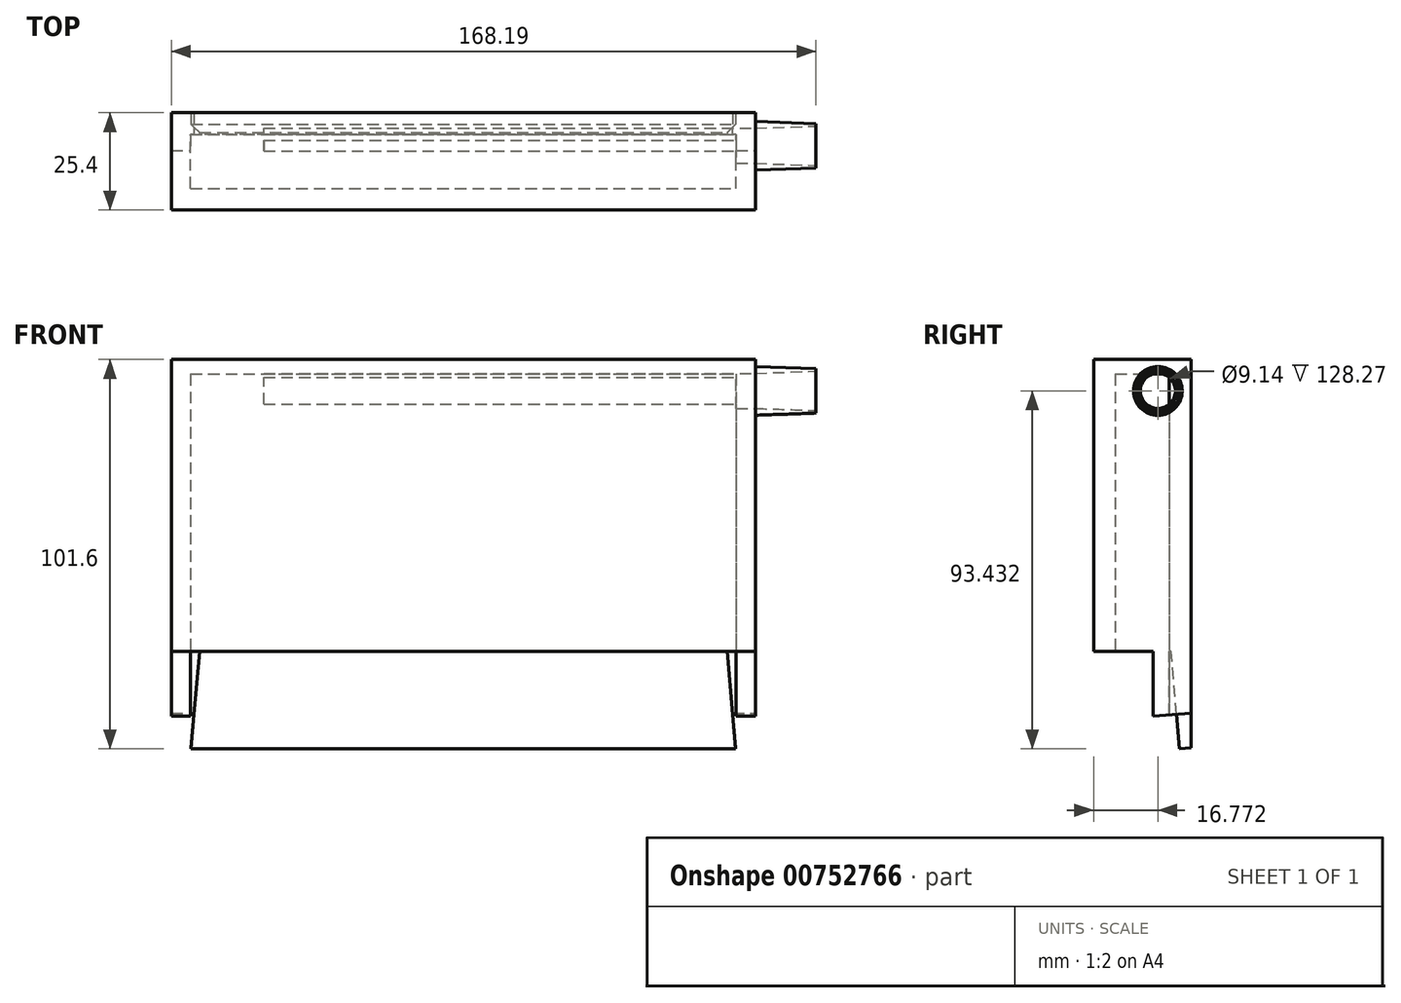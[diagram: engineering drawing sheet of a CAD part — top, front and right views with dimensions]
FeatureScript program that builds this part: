
annotation { "Feature Type Name" : "Feature", "Feature Type Description" : "" }
export const myFeature = defineFeature(function(context is Context, id is Id, definition is map)
    precondition{}
    {
        {
            var Q0;
            Q0=qCreatedBy(makeId("Front.planeOp"),FACE);
            var sketch = newSketch(context, id + "F0", { "sketchPlane" : qUnion([Q0])});
            skLineSegment(sketch, "E0.bottom", {"start": v(-76.2, 38.1) * mm, "end": v(76.2, 38.1) * mm});
            skLineSegment(sketch, "E0.top", {"start": v(-76.2, -38.1) * mm, "end": v(76.2, -38.1) * mm});
            skLineSegment(sketch, "E0.left", {"start": v(-76.2, 38.1) * mm, "end": v(-76.2, -38.1) * mm});
            skLineSegment(sketch, "E0.right", {"start": v(76.2, 38.1) * mm, "end": v(76.2, -38.1) * mm});
            skPoint(sketch, "E0.middle", {"position": v(0, 0) * mm});
            skLineSegment(sketch, "E1", {"start": v(-76.2, -34.16) * mm, "end": v(76.2, -34.16) * mm});
            skSolve(sketch);
        }
        {
            var Q0;
            {var subQ0=sQuery(id+"F0.wireOp",EDGE,"E0.bottom");Q0=makeQuery(id+"F0.imprint","IMPRINT",FACE,{"disambiguationData":[TD([[makeQuery(id+"F0.imprint","IMPRINT",EDGE,{"derivedFrom":subQ0}),-1.0]])]});}
            var Q1;
            {var subQ0=sQuery(id+"F0.wireOp",EDGE,"E0.top");Q1=makeQuery(id+"F0.imprint","IMPRINT",FACE,{"disambiguationData":[TD([[makeQuery(id+"F0.imprint","IMPRINT",EDGE,{"derivedFrom":subQ0}),1.0]])]});}
            extrude(context, id + "F1", {"entities" : qUnion([Q0, Q1]), "depth" : 25.4 * mm, "offsetDistance" : 25.4 * mm});
        }
        {
            var Q0;
            Q0=makeQuery(id+"F1.opExtrude","SWEPT_FACE",FACE,{"disambiguationData":[OSD([sQuery(id+"F0.wireOp",EDGE,"E0.right")])]});
            var sketch = newSketch(context, id + "F2", { "sketchPlane" : qUnion([Q0])});
            skCircle(sketch, "E2", {"center": v(-8.63, 29.93) * mm, "radius": 6.35 * mm});
            skCircle(sketch, "E3", {"center": v(-8.63, 29.93) * mm, "radius": 4.57 * mm});
            skSolve(sketch);
        }
        {
            var Q0;
            Q0=makeQuery(id+"F2.imprint","IMPRINT",FACE,{"disambiguationData":[TD([[makeQuery(id+"F2.imprint","IMPRINT",EDGE,{"derivedFrom":sQuery(id+"F2.wireOp",EDGE,"E3")}),1.0]])]});
            extrude(context, id + "F3", {"entities" : qUnion([Q0]), "operationType" : NewBodyOperationType.REMOVE, "oppositeDirection" : true, "depth" : 128.27 * mm, "offsetDistance" : 25.4 * mm});
        }
        {
            var Q0;
            Q0 = qSketchRegion(id + "F2", true);
            extrude(context, id + "F4", {"entities" : qUnion([Q0]), "operationType" : NewBodyOperationType.ADD, "depth" : 25.4 * mm, "offsetDistance" : 25.4 * mm, "hasDraft" : true, "draftAngle" : 2 * degree, "draftPullDirection" : true});
        }
        {
            var Q0;
            Q0=makeQuery(id+"F1.opExtrude","SWEPT_FACE",FACE,{"disambiguationData":[OSD([sQuery(id+"F0.wireOp",EDGE,"E0.top")])]});
            var sketch = newSketch(context, id + "F5", { "sketchPlane" : qUnion([Q0])});
            skLineSegment(sketch, "E4.bottom", {"start": v(-71.2, 19.71) * mm, "end": v(71.2, 19.71) * mm});
            skLineSegment(sketch, "E4.top", {"start": v(-71.2, 5.69) * mm, "end": v(71.2, 5.69) * mm});
            skLineSegment(sketch, "E4.left", {"start": v(-71.2, 19.71) * mm, "end": v(-71.2, 5.69) * mm});
            skLineSegment(sketch, "E4.right", {"start": v(71.2, 19.71) * mm, "end": v(71.2, 5.69) * mm});
            skPoint(sketch, "E4.middle", {"position": v(0, 12.7) * mm});
            skPoint(sketch, "E4.middle.positionSnap0", {"position": v(-76.2, 12.7) * mm});
            skPoint(sketch, "E4.centerSnap0", {"position": v(-76.2, 12.7) * mm});
            skSolve(sketch);
        }
        {
            var Q0;
            Q0=makeQuery(id+"F5.imprint","IMPRINT",FACE,{"disambiguationData":[TD([[makeQuery(id+"F5.imprint","IMPRINT",EDGE,{"derivedFrom":sQuery(id+"F5.wireOp",EDGE,"E4.bottom")}),-1.0]])]});
            extrude(context, id + "F6", {"entities" : qUnion([Q0]), "operationType" : NewBodyOperationType.REMOVE, "oppositeDirection" : true, "depth" : 72.39 * mm, "offsetDistance" : 25.4 * mm});
        }
        {
            var Q0;
            Q0=qCreatedBy(makeId("Front.planeOp"),FACE);
            var sketch = newSketch(context, id + "F7", { "sketchPlane" : qUnion([Q0])});
            skLineSegment(sketch, "E5.bottom", {"start": v(92, 10.22) * mm, "end": v(133.43, 10.22) * mm});
            skLineSegment(sketch, "E5.top", {"start": v(92, 52.24) * mm, "end": v(133.43, 52.24) * mm});
            skLineSegment(sketch, "E5.left", {"start": v(92, 10.22) * mm, "end": v(92, 52.24) * mm});
            skLineSegment(sketch, "E5.right", {"start": v(133.43, 10.22) * mm, "end": v(133.43, 52.24) * mm});
            skPoint(sketch, "E5.middle", {"position": v(112.71, 31.23) * mm});
            skSolve(sketch);
        }
        {
            var Q0;
            Q0=makeQuery(id+"F7.imprint","IMPRINT",FACE,{"disambiguationData":[TD([[makeQuery(id+"F7.imprint","IMPRINT",EDGE,{"derivedFrom":sQuery(id+"F7.wireOp",EDGE,"E5.bottom")}),1.0]])]});
            extrude(context, id + "F8", {"entities" : qUnion([Q0]), "operationType" : NewBodyOperationType.REMOVE, "endBound" : BoundingType.SYMMETRIC, "depth" : 68.58 * mm, "offsetDistance" : 25.4 * mm});
        }
        {
            var Q0;
            Q0=makeQuery(id+"F1.opExtrude","SWEPT_FACE",FACE,{"disambiguationData":[OSD([sQuery(id+"F0.wireOp",EDGE,"E0.top")])]});
            var sketch = newSketch(context, id + "F9", { "sketchPlane" : qUnion([Q0])});
            skLineSegment(sketch, "E6", {"start": v(-76.2, 9.88) * mm, "end": v(76.2, 9.88) * mm});
            skLineSegment(sketch, "E7", {"start": v(76.2, 9.88) * mm, "end": v(76.2, 0) * mm});
            skLineSegment(sketch, "E8", {"start": v(76.2, 0) * mm, "end": v(-76.2, 0) * mm});
            skLineSegment(sketch, "E9", {"start": v(-76.2, 0) * mm, "end": v(-76.2, 9.88) * mm});
            skSolve(sketch);
        }
        {
            var Q0;
            {var subQ0=sQuery(id+"F9.wireOp",EDGE,"E7");Q0=makeQuery(id+"F9.imprint","IMPRINT",FACE,{"disambiguationData":[TD([[makeQuery(id+"F9.imprint","IMPRINT",EDGE,{"derivedFrom":subQ0}),-1.0]])]});}
            var Q1;
            {var subQ5=makeQuery(id+"F6.boolean.opBoolean","COPY",EDGE,{"derivedFrom":makeQuery(id+"F6.opExtrude","CAP_EDGE",EDGE,{"disambiguationData":[OSD([sQuery(id+"F5.wireOp",EDGE,"E4.top")])],"isStart":true})});Q1=makeQuery(id+"F9.imprint","IMPRINT",FACE,{"disambiguationData":[TD([[makeQuery(id+"F9.imprint","IMPRINT",EDGE,{"derivedFrom":subQ5}),1.0]])]});}
            extrude(context, id + "F10", {"entities" : qUnion([Q0, Q1]), "operationType" : NewBodyOperationType.ADD, "depth" : 25.4 * mm, "offsetDistance" : 25.4 * mm});
        }
        {
            var Q0;
            Q0=makeQuery(id+"F10.opExtrude","CAP_FACE",FACE,{"disambiguationData":[OSD([sQuery(id+"F9.wireOp",EDGE,"E6"),sQuery(id+"F9.wireOp",EDGE,"E7"),sQuery(id+"F9.wireOp",EDGE,"E8"),sQuery(id+"F9.wireOp",EDGE,"E9")])],"isStart":false});
            var sketch = newSketch(context, id + "F11", { "sketchPlane" : qUnion([Q0])});
            skLineSegment(sketch, "E10.bottom", {"start": v(-71.06, 16.8) * mm, "end": v(71.06, 16.8) * mm});
            skLineSegment(sketch, "E10.top", {"start": v(-71.06, 2.96) * mm, "end": v(71.06, 2.96) * mm});
            skLineSegment(sketch, "E10.left", {"start": v(-71.06, 16.8) * mm, "end": v(-71.06, 2.96) * mm});
            skLineSegment(sketch, "E10.right", {"start": v(71.06, 16.8) * mm, "end": v(71.06, 2.96) * mm});
            skPoint(sketch, "E10.middle", {"position": v(0, 9.88) * mm});
            skSolve(sketch);
        }
        {
            var Q0;
            {var subQ0=sQuery(id+"F11.wireOp",EDGE,"E10.top");Q0=makeQuery(id+"F11.imprint","IMPRINT",FACE,{"disambiguationData":[TD([[makeQuery(id+"F11.imprint","IMPRINT",EDGE,{"derivedFrom":subQ0}),1.0]])]});}
            var Q1;
            {var subQ0=sQuery(id+"F11.wireOp",EDGE,"E10.bottom");Q1=makeQuery(id+"F11.imprint","IMPRINT",FACE,{"disambiguationData":[TD([[makeQuery(id+"F11.imprint","IMPRINT",EDGE,{"derivedFrom":subQ0}),-1.0]])]});}
            extrude(context, id + "F12", {"entities" : qUnion([Q0, Q1]), "operationType" : NewBodyOperationType.REMOVE, "oppositeDirection" : true, "depth" : 25.4 * mm, "offsetDistance" : 25.4 * mm, "hasDraft" : true, "draftAngle" : 5 * degree, "draftPullDirection" : true});
        }
        {
            var Q0;
            Q0=makeQuery(id+"F12.boolean.opBoolean","COPY",FACE,{"derivedFrom":makeQuery(id+"F12.opExtrude","SWEPT_FACE",FACE,{"disambiguationData":[OSD([sQuery(id+"F11.wireOp",EDGE,"E10.top")])]})});
            var sketch = newSketch(context, id + "F13", { "sketchPlane" : qUnion([Q0])});
            skLineSegment(sketch, "E11.bottom", {"start": v(-92.4, -53.9) * mm, "end": v(92.4, -53.9) * mm});
            skLineSegment(sketch, "E11.top", {"start": v(-92.4, -129.4) * mm, "end": v(92.4, -129.4) * mm});
            skLineSegment(sketch, "E11.left", {"start": v(-92.4, -53.9) * mm, "end": v(-92.4, -129.4) * mm});
            skLineSegment(sketch, "E11.right", {"start": v(92.4, -53.9) * mm, "end": v(92.4, -129.4) * mm});
            skPoint(sketch, "E11.middle", {"position": v(0, -91.66) * mm});
            skSolve(sketch);
        }
        {
            var Q0;
            Q0=makeQuery(id+"F13.imprint","IMPRINT",FACE,{"disambiguationData":[TD([[makeQuery(id+"F13.imprint","IMPRINT",EDGE,{"derivedFrom":sQuery(id+"F13.wireOp",EDGE,"E11.top")}),1.0]])]});
            var Q1;
            {var subQ1=sQuery(id+"F11.wireOp",EDGE,"E10.top");var subQ6=makeQuery(id+"F12.boolean.opBoolean","COPY",EDGE,{"derivedFrom":makeQuery(id+"F12.opExtrude","CAP_EDGE",EDGE,{"disambiguationData":[OSD([subQ1])],"isStart":true})});Q1=makeQuery(id+"F13.imprint","IMPRINT",FACE,{"disambiguationData":[TD([[makeQuery(id+"F13.imprint","IMPRINT",EDGE,{"derivedFrom":subQ6}),1.0]])]});}
            extrude(context, id + "F14", {"entities" : qUnion([Q0, Q1]), "operationType" : NewBodyOperationType.REMOVE, "endBound" : BoundingType.SYMMETRIC, "oppositeDirection" : true, "depth" : 25.4 * mm, "offsetDistance" : 25.4 * mm});
        }
    });
